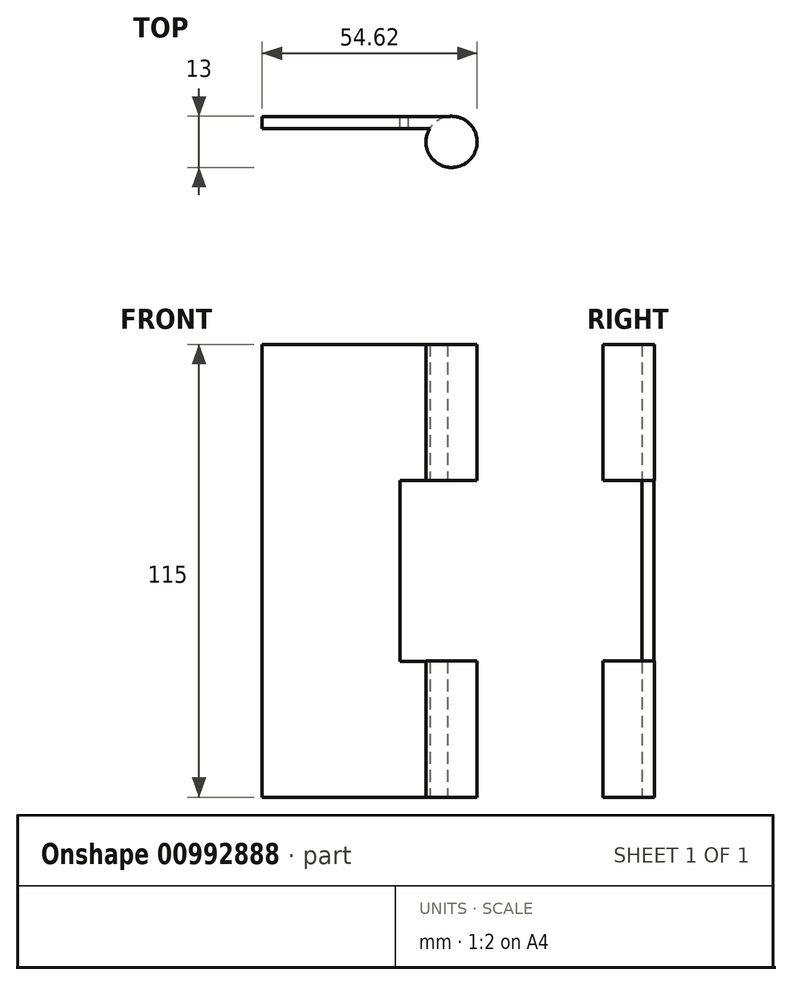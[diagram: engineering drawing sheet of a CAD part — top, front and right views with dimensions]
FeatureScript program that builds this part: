
annotation { "Feature Type Name" : "Feature", "Feature Type Description" : "" }
export const myFeature = defineFeature(function(context is Context, id is Id, definition is map)
    precondition{}
    {
        {
            var Q0;
            Q0=qCreatedBy(makeId("Front.planeOp"),FACE);
            var sketch = newSketch(context, id + "F0", { "sketchPlane" : qUnion([Q0])});
            skLineSegment(sketch, "E0", {"start": v(0, 0) * mm, "end": v(0, 115) * mm});
            skLineSegment(sketch, "E1", {"start": v(0, 115) * mm, "end": v(48, 115) * mm});
            skLineSegment(sketch, "E2", {"start": v(48, 115) * mm, "end": v(48, 80.5) * mm});
            skLineSegment(sketch, "E3", {"start": v(48, 80.5) * mm, "end": v(35, 80.5) * mm});
            skLineSegment(sketch, "E4", {"start": v(35, 80.5) * mm, "end": v(35, 34.5) * mm});
            skLineSegment(sketch, "E5", {"start": v(35, 34.5) * mm, "end": v(48, 34.5) * mm});
            skLineSegment(sketch, "E6", {"start": v(48, 34.5) * mm, "end": v(48, 0) * mm});
            skLineSegment(sketch, "E7", {"start": v(48, 0) * mm, "end": v(0, 0) * mm});
            skSolve(sketch);
        }
        {
            var Q0;
            Q0=makeQuery(id+"F0.imprint","IMPRINT",FACE,{"disambiguationData":[TD([[makeQuery(id+"F0.imprint","IMPRINT",EDGE,{"derivedFrom":sQuery(id+"F0.wireOp",EDGE,"E0")}),-1.0]])]});
            extrude(context, id + "F1", {"entities" : qUnion([Q0]), "depth" : 3 * mm, "offsetDistance" : 25 * mm});
        }
        {
            var Q0;
            Q0=qCreatedBy(makeId("Top.planeOp"),FACE);
            var sketch = newSketch(context, id + "F2", { "sketchPlane" : qUnion([Q0])});
            skCircle(sketch, "E8", {"center": v(48.12, -6.42) * mm, "radius": 6.5 * mm});
            skSolve(sketch);
        }
        {
            var Q0;
            Q0=makeQuery(id+"F2.imprint","IMPRINT",FACE,{"disambiguationData":[TD([[makeQuery(id+"F2.imprint","IMPRINT",EDGE,{"derivedFrom":sQuery(id+"F2.wireOp",EDGE,"E8")}),1.0]])]});
            extrude(context, id + "F3", {"entities" : qUnion([Q0]), "operationType" : NewBodyOperationType.ADD, "depth" : 115 * mm, "offsetDistance" : 25 * mm});
        }
        {
            var Q0;
            Q0=qCreatedBy(makeId("Front.planeOp"),FACE);
            var sketch = newSketch(context, id + "F4", { "sketchPlane" : qUnion([Q0])});
            skLineSegment(sketch, "E9.bottom", {"start": v(37.12, 80.52) * mm, "end": v(65.5, 80.52) * mm});
            skLineSegment(sketch, "E9.top", {"start": v(37.12, 34.58) * mm, "end": v(65.5, 34.58) * mm});
            skLineSegment(sketch, "E9.left", {"start": v(37.12, 80.52) * mm, "end": v(37.12, 34.58) * mm});
            skLineSegment(sketch, "E9.right", {"start": v(65.5, 80.52) * mm, "end": v(65.5, 34.58) * mm});
            skSolve(sketch);
        }
        {
            var Q0;
            Q0 = qSketchRegion(id + "F4", true);
            extrude(context, id + "F5", {"entities" : qUnion([Q0]), "operationType" : NewBodyOperationType.REMOVE, "depth" : 25 * mm, "offsetDistance" : 25 * mm});
        }
        {
            var Q0;
            Q0 = qSketchRegion(id + "F4", true);
            extrude(context, id + "F6", {"entities" : qUnion([Q0]), "operationType" : NewBodyOperationType.REMOVE, "oppositeDirection" : true, "depth" : 25 * mm, "offsetDistance" : 25 * mm});
        }
    });
